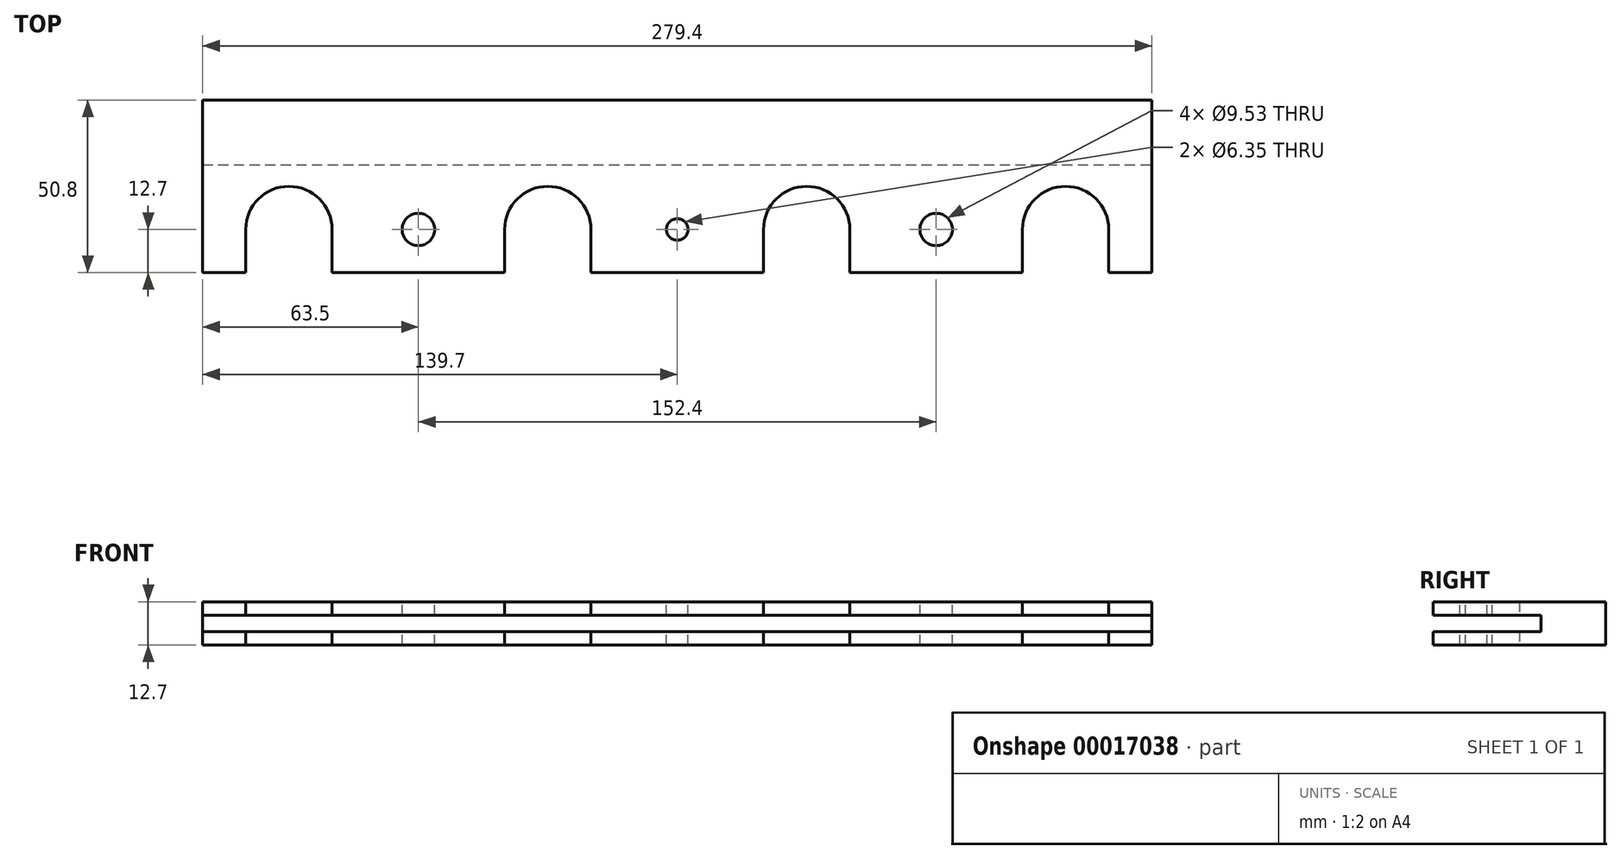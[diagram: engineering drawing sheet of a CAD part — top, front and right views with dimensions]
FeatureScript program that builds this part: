
annotation { "Feature Type Name" : "Feature", "Feature Type Description" : "" }
export const myFeature = defineFeature(function(context is Context, id is Id, definition is map)
    precondition{}
    {
        {
            var Q0;
            Q0=qCreatedBy(makeId("Top.planeOp"),FACE);
            var sketch = newSketch(context, id + "F0", { "sketchPlane" : qUnion([Q0])});
            skLineSegment(sketch, "E0.bottom", {"start": v(139.7, 25.4) * mm, "end": v(-139.7, 25.4) * mm});
            skLineSegment(sketch, "E0.top", {"start": v(139.7, -25.4) * mm, "end": v(127, -25.4) * mm});
            skLineSegment(sketch, "E0.left", {"start": v(139.7, 25.4) * mm, "end": v(139.7, -25.4) * mm});
            skLineSegment(sketch, "E0.right", {"start": v(-139.7, 25.4) * mm, "end": v(-139.7, -25.4) * mm});
            skPoint(sketch, "E0.middle", {"position": v(0, 0) * mm});
            skLineSegment(sketch, "E1", {"start": v(-139.7, -12.7) * mm, "end": v(-127, -12.7) * mm});
            skLineSegment(sketch, "E2", {"start": v(114.3, 0) * mm, "end": v(114.3, -41.2) * mm});
            skLineSegment(sketch, "E3", {"start": v(38.1, -4.36) * mm, "end": v(38.1, -40.47) * mm});
            skLineSegment(sketch, "E4", {"start": v(-38.1, -5.08) * mm, "end": v(-38.1, -45.52) * mm});
            skLineSegment(sketch, "E5", {"start": v(-114.3, -5.08) * mm, "end": v(-114.3, -50.94) * mm});
            skArc(sketch, "E6", {"start": v(127, -12.7) * mm, "mid": v(114.3, 0) * mm, "end": v(101.6, -12.7) * mm});
            skArc(sketch, "E7", {"start": v(50.8, -12.7) * mm, "mid": v(38.1, 0) * mm, "end": v(25.4, -12.7) * mm});
            skArc(sketch, "E8", {"start": v(-25.4, -12.7) * mm, "mid": v(-38.1, 0) * mm, "end": v(-50.8, -12.7) * mm});
            skArc(sketch, "E9", {"start": v(-101.6, -12.7) * mm, "mid": v(-114.3, 0) * mm, "end": v(-127, -12.7) * mm});
            skLineSegment(sketch, "E10", {"start": v(-101.6, -12.7) * mm, "end": v(-101.6, -25.4) * mm});
            skLineSegment(sketch, "E11", {"start": v(-127, -12.7) * mm, "end": v(-127, -25.4) * mm});
            skLineSegment(sketch, "E12.trimOffspring", {"start": v(-127, -25.4) * mm, "end": v(-139.7, -25.4) * mm});
            skLineSegment(sketch, "E13.trimOffspring", {"start": v(-101.6, -12.7) * mm, "end": v(-50.8, -12.7) * mm});
            skLineSegment(sketch, "E14", {"start": v(-25.4, -12.7) * mm, "end": v(-25.4, -32.3) * mm});
            skLineSegment(sketch, "E15", {"start": v(-50.8, -12.7) * mm, "end": v(-50.8, -25.4) * mm});
            skLineSegment(sketch, "E16", {"start": v(25.4, -12.7) * mm, "end": v(25.4, -25.4) * mm});
            skLineSegment(sketch, "E17", {"start": v(50.8, -12.7) * mm, "end": v(50.8, -25.4) * mm});
            skLineSegment(sketch, "E18", {"start": v(101.6, -12.7) * mm, "end": v(101.6, -25.4) * mm});
            skLineSegment(sketch, "E19", {"start": v(127, -12.7) * mm, "end": v(127, -25.4) * mm});
            skLineSegment(sketch, "E20.trimOffspring", {"start": v(25.4, -25.4) * mm, "end": v(-25.4, -25.4) * mm});
            skLineSegment(sketch, "E21.trimOffspring", {"start": v(-25.4, -12.7) * mm, "end": v(25.4, -12.7) * mm});
            skLineSegment(sketch, "E22.trimOffspring", {"start": v(-50.8, -25.4) * mm, "end": v(-101.6, -25.4) * mm});
            skLineSegment(sketch, "E23.trimOffspring", {"start": v(50.8, -12.7) * mm, "end": v(101.6, -12.7) * mm});
            skLineSegment(sketch, "E24.trimOffspring", {"start": v(127, -12.7) * mm, "end": v(139.7, -12.7) * mm});
            skLineSegment(sketch, "E25.trimOffspring", {"start": v(101.6, -25.4) * mm, "end": v(50.8, -25.4) * mm});
            skSolve(sketch);
        }
        {
            var Q0;
            {var subQ4=sQuery(id+"F0.wireOp",EDGE,"E0.bottom");Q0=makeQuery(id+"F0.imprint","IMPRINT",FACE,{"disambiguationData":[TD([[makeQuery(id+"F0.imprint","IMPRINT",EDGE,{"derivedFrom":subQ4}),1.0]])]});}
            var Q1;
            {var subQ0=sQuery(id+"F0.wireOp",EDGE,"E0.top");Q1=makeQuery(id+"F0.imprint","IMPRINT",FACE,{"disambiguationData":[TD([[makeQuery(id+"F0.imprint","IMPRINT",EDGE,{"derivedFrom":subQ0}),-1.0]])]});}
            var Q2;
            Q2=makeQuery(id+"F0.imprint","IMPRINT",FACE,{"disambiguationData":[TD([[makeQuery(id+"F0.imprint","IMPRINT",EDGE,{"derivedFrom":sQuery(id+"F0.wireOp",EDGE,"E16")}),-1.0]])]});
            var Q3;
            Q3=makeQuery(id+"F0.imprint","IMPRINT",FACE,{"disambiguationData":[TD([[makeQuery(id+"F0.imprint","IMPRINT",EDGE,{"derivedFrom":sQuery(id+"F0.wireOp",EDGE,"E17")}),1.0]])]});
            var Q4;
            Q4=makeQuery(id+"F0.imprint","IMPRINT",FACE,{"disambiguationData":[TD([[makeQuery(id+"F0.imprint","IMPRINT",EDGE,{"derivedFrom":sQuery(id+"F0.wireOp",EDGE,"E10")}),1.0]])]});
            var Q5;
            {var subQ2=sQuery(id+"F0.wireOp",EDGE,"E1");Q5=makeQuery(id+"F0.imprint","IMPRINT",FACE,{"disambiguationData":[TD([[makeQuery(id+"F0.imprint","IMPRINT",EDGE,{"derivedFrom":subQ2}),-1.0]])]});}
            extrude(context, id + "F1", {"entities" : qUnion([Q0, Q1, Q2, Q3, Q4, Q5]), "depth" : 12.7 * mm});
        }
        {
            var Q0;
            Q0=makeQuery(id+"F1.opExtrude","SWEPT_FACE",FACE,{"disambiguationData":[OSD([sQuery(id+"F0.wireOp",EDGE,"E0.left")])]});
            var sketch = newSketch(context, id + "F2", { "sketchPlane" : qUnion([Q0])});
            skLineSegment(sketch, "E26.bottom", {"start": v(6.35, 8.76) * mm, "end": v(-57.15, 8.76) * mm});
            skLineSegment(sketch, "E26.top", {"start": v(6.35, 3.94) * mm, "end": v(-57.15, 3.94) * mm});
            skLineSegment(sketch, "E26.left", {"start": v(6.35, 8.76) * mm, "end": v(6.35, 3.94) * mm});
            skLineSegment(sketch, "E26.right", {"start": v(-57.15, 8.76) * mm, "end": v(-57.15, 3.94) * mm});
            skPoint(sketch, "E26.middle", {"position": v(-25.4, 6.35) * mm});
            skSolve(sketch);
        }
        {
            var Q0;
            Q0 = qSketchRegion(id + "F2", true);
            extrude(context, id + "F3", {"entities" : qUnion([Q0]), "operationType" : NewBodyOperationType.REMOVE, "endBound" : BoundingType.THROUGH_ALL, "oppositeDirection" : true, "depth" : 25.4 * mm});
        }
        {
            var Q0;
            Q0=makeQuery(id+"F1.opExtrude","CAP_FACE",FACE,{"disambiguationData":[OSD([sQuery(id+"F0.wireOp",EDGE,"E0.bottom"),sQuery(id+"F0.wireOp",EDGE,"E0.top"),sQuery(id+"F0.wireOp",EDGE,"E0.left"),sQuery(id+"F0.wireOp",EDGE,"E0.right"),sQuery(id+"F0.wireOp",EDGE,"E6"),sQuery(id+"F0.wireOp",EDGE,"E7"),sQuery(id+"F0.wireOp",EDGE,"E8"),sQuery(id+"F0.wireOp",EDGE,"E9"),sQuery(id+"F0.wireOp",EDGE,"E10"),sQuery(id+"F0.wireOp",EDGE,"E11"),sQuery(id+"F0.wireOp",EDGE,"E12.trimOffspring"),sQuery(id+"F0.wireOp",EDGE,"E14"),sQuery(id+"F0.wireOp",EDGE,"E15"),sQuery(id+"F0.wireOp",EDGE,"E16"),sQuery(id+"F0.wireOp",EDGE,"E17"),sQuery(id+"F0.wireOp",EDGE,"E18"),sQuery(id+"F0.wireOp",EDGE,"E19"),sQuery(id+"F0.wireOp",EDGE,"E20.trimOffspring"),sQuery(id+"F0.wireOp",EDGE,"E22.trimOffspring"),sQuery(id+"F0.wireOp",EDGE,"E25.trimOffspring")])],"isStart":false});
            var sketch = newSketch(context, id + "F4", { "sketchPlane" : qUnion([Q0])});
            skLineSegment(sketch, "E27", {"start": v(-38.1, -12.7) * mm, "end": v(38.1, -12.7) * mm});
            skCircle(sketch, "E28", {"center": v(0, -12.7) * mm, "radius": 3.18 * mm});
            skCircle(sketch, "E29", {"center": v(76.2, -12.7) * mm, "radius": 4.76 * mm});
            skCircle(sketch, "E30", {"center": v(-76.2, -12.7) * mm, "radius": 4.76 * mm});
            skSolve(sketch);
        }
        {
            var Q0;
            Q0 = qSketchRegion(id + "F4", true);
            extrude(context, id + "F5", {"entities" : qUnion([Q0]), "operationType" : NewBodyOperationType.REMOVE, "oppositeDirection" : true, "depth" : 25.4 * mm});
        }
    });
